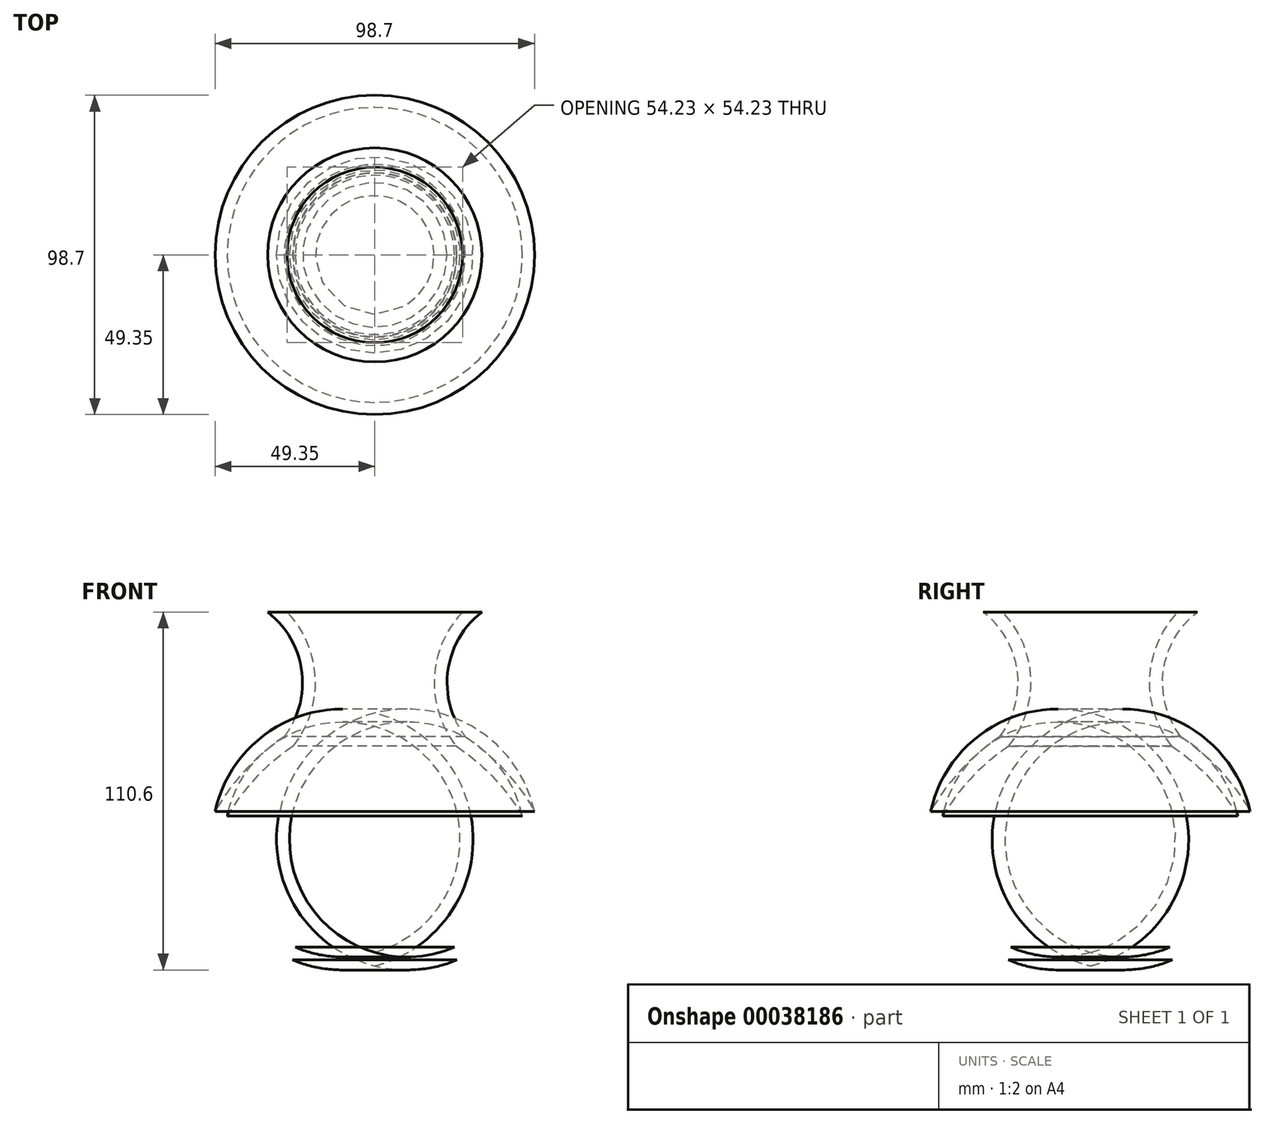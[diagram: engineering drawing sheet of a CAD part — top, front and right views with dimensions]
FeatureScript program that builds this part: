
annotation { "Feature Type Name" : "Feature", "Feature Type Description" : "" }
export const myFeature = defineFeature(function(context is Context, id is Id, definition is map)
    precondition{}
    {
        {
            var Q0;
            Q0=qCreatedBy(makeId("Front.planeOp"),FACE);
            var sketch = newSketch(context, id + "F0", { "sketchPlane" : qUnion([Q0])});
            skLineSegment(sketch, "E0", {"start": v(0, 41.5) * mm, "end": v(33.09, 41.5) * mm});
            skArc(sketch, "E1", {"start": v(33.09, 41.5) * mm, "mid": v(22.58, 23.3) * mm, "end": v(27.95, 3) * mm});
            skArc(sketch, "E2", {"start": v(49.35, -20.1) * mm, "mid": v(39.99, -7.32) * mm, "end": v(27.95, 3) * mm});
            skArc(sketch, "E3", {"start": v(25.39, -66.03) * mm, "mid": v(45.72, -47.43) * mm, "end": v(49.35, -20.1) * mm});
            skLineSegment(sketch, "E4", {"start": v(25.39, -66.03) * mm, "end": v(0, -66.03) * mm});
            skLineSegment(sketch, "E5", {"start": v(0, 41.5) * mm, "end": v(0, -66.03) * mm});
            skSolve(sketch);
        }
        {
            var Q0;
            Q0=makeQuery(id+"F0.imprint","IMPRINT",FACE,{"disambiguationData":[TD([[makeQuery(id+"F0.imprint","IMPRINT",EDGE,{"derivedFrom":sQuery(id+"F0.wireOp",EDGE,"E0")}),-1.0]])]});
            var Q1;
            Q1=sQuery(id+"F0.wireOp",EDGE,"E5");
            revolve(context, id + "F1", {"entities" : qUnion([Q0]), "axis" : qUnion([Q1]), "revolveType" : RevolveType.FULL});
        }
        {
            var Q0;
            Q0=makeQuery(id+"F1.opRevolve","SWEPT_FACE",FACE,{"disambiguationData":[OSD([sQuery(id+"F0.wireOp",EDGE,"E0")])]});
            shell(context, id + "F2", {"entities" : qUnion([Q0]), "thickness" : 4 * mm});
        }
    });
